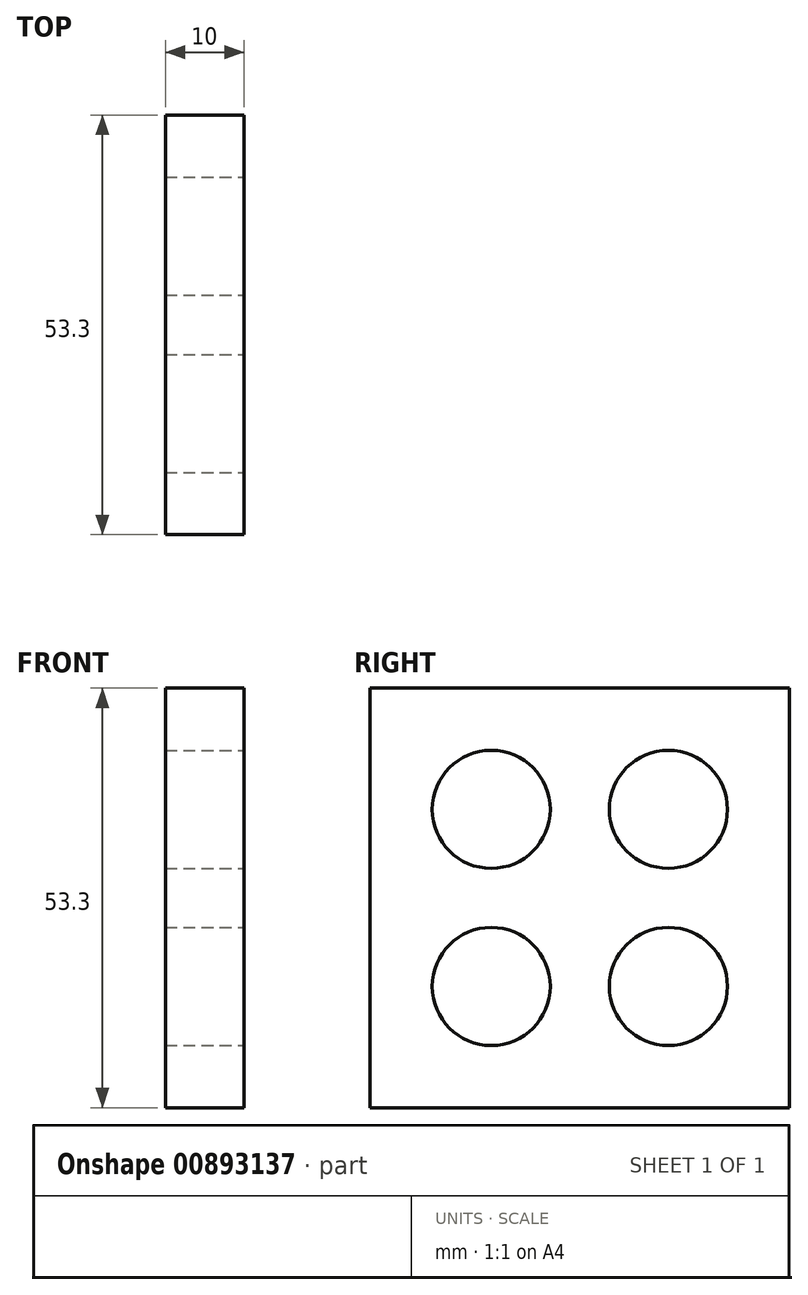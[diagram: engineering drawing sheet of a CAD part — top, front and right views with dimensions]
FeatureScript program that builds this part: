
annotation { "Feature Type Name" : "Feature", "Feature Type Description" : "" }
export const myFeature = defineFeature(function(context is Context, id is Id, definition is map)
    precondition{}
    {
        {
            var Q0;
            Q0=qCreatedBy(makeId("Right.planeOp"),FACE);
            var sketch = newSketch(context, id + "F0", { "sketchPlane" : qUnion([Q0])});
            skCircle(sketch, "E0", {"center": v(0, 0) * mm, "radius": 7.5 * mm});
            skCircle(sketch, "E1", {"center": v(0, 22.5) * mm, "radius": 7.5 * mm});
            skCircle(sketch, "E2.MirrorC", {"center": v(22.5, 22.5) * mm, "radius": 7.5 * mm});
            skCircle(sketch, "E3.MirrorC", {"center": v(22.5, 0) * mm, "radius": 7.5 * mm});
            skPoint(sketch, "E4.endSnap0", {"position": v(3.75, 0) * mm});
            skPoint(sketch, "E4.endSnap1", {"position": v(0, 3.75) * mm});
            skPoint(sketch, "E5.endSnap0", {"position": v(3.75, 22.5) * mm});
            skLineSegment(sketch, "E6.0", {"start": v(0, 37.9) * mm, "end": v(22.5, 37.9) * mm});
            skLineSegment(sketch, "E7.0", {"start": v(22.5, -15.4) * mm, "end": v(0, -15.4) * mm});
            skLineSegment(sketch, "E8.0", {"start": v(-15.4, 15) * mm, "end": v(-15.4, 7.5) * mm});
            skLineSegment(sketch, "E9.0", {"start": v(37.9, 22.5) * mm, "end": v(37.9, 0) * mm});
            skLineSegment(sketch, "E10", {"start": v(22.5, 37.9) * mm, "end": v(37.9, 37.9) * mm});
            skLineSegment(sketch, "E11", {"start": v(37.9, 37.9) * mm, "end": v(37.9, 22.5) * mm});
            skLineSegment(sketch, "E12", {"start": v(0, 37.9) * mm, "end": v(-15.4, 37.9) * mm});
            skLineSegment(sketch, "E13", {"start": v(-15.4, 37.9) * mm, "end": v(-15.4, 15) * mm});
            skLineSegment(sketch, "E14", {"start": v(0, -15.4) * mm, "end": v(-15.4, -15.4) * mm});
            skLineSegment(sketch, "E15", {"start": v(-15.4, -15.4) * mm, "end": v(-15.4, 7.5) * mm});
            skLineSegment(sketch, "E16", {"start": v(22.5, -15.4) * mm, "end": v(37.9, -15.4) * mm});
            skLineSegment(sketch, "E17", {"start": v(37.9, -15.4) * mm, "end": v(37.9, 0) * mm});
            skSolve(sketch);
        }
        {
            var Q0;
            Q0=makeQuery(id+"F0.imprint","IMPRINT",FACE,{"disambiguationData":[TD([[makeQuery(id+"F0.imprint","IMPRINT",EDGE,{"derivedFrom":sQuery(id+"F0.wireOp",EDGE,"E0")}),-1.0]])]});
            extrude(context, id + "F1", {"entities" : qUnion([Q0]), "oppositeDirection" : true, "depth" : 10 * mm, "offsetDistance" : 25 * mm});
        }
    });
